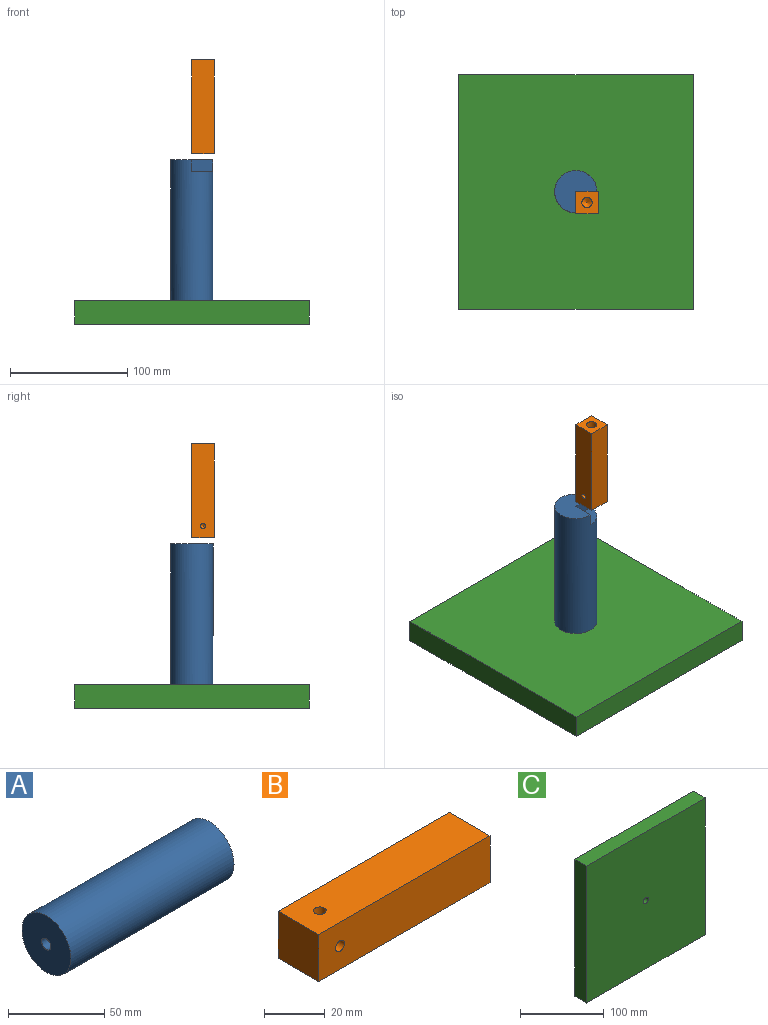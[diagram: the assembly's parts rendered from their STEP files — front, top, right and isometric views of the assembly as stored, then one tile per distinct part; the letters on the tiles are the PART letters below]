
ASSEMBLY  parts=3 mates=4
PART A: 8 faces, bbox 120x36x36 mm
  f0: cylinder r=18mm len=120mm, axis (-1,0,0), area 13288.9mm2, adj f1,f2,f5,f6,f7
  f1: plane 36x36mm, normal (-1,0,0), area 981.6mm2, adj f0,f4
  f2: plane 36x36mm, normal (1,0,0), area 763.4mm2, adj f0,f5,f6
  f3: cone r=0mm half-angle=59deg, axis (-1,0,0), area 42.4mm2, adj f4
  f4: cylinder r=3.4mm len=15.75mm, axis (-1,0,0), area 336.5mm2, adj f1,f3
  f5: plane 18x10mm, normal (0,1,0), area 180mm2, adj f0,f2,f6,f7
  f6: plane 18x10mm, normal (0,0,-1), area 180mm2, adj f0,f2,f5,f7
  f7: plane 18x18mm, normal (1,0,0), area 254.5mm2, adj f0,f5,f6
PART B: 14 faces, bbox 80x19x19 mm
  f0: plane 80x19mm, normal (0,0,1), area 1506.1mm2, adj f1,f3,f4,f5,f11
  f1: plane 19x19mm, normal (-1,0,0), area 361mm2, adj f0,f2,f4,f5
  f2: plane 80x19mm, normal (0,0,-1), area 1520mm2, adj f1,f3,f4,f5
  f3: plane 19x19mm, normal (1,0,0), area 300.2mm2, adj f0,f2,f4,f5,f7
  f4: plane 80x19mm, normal (0,-1,0), area 1506.1mm2, adj f0,f1,f2,f3,f10
  f5: plane 80x19mm, normal (0,1,0), area 1520mm2, adj f0,f1,f2,f3
  f6: cone r=0mm half-angle=59deg, axis (1,0,0), area 71mm2, adj f7
  f7: cylinder r=4.4mm len=15.75mm, axis (1,0,0), area 435.4mm2, adj f3,f6
  f8: cylinder r=2.1mm len=4.9mm, axis (0,0,1), area 47mm2, adj f9,f10,f12
  f9: cone r=0mm half-angle=59deg, axis (0,0,1), area 16.2mm2, adj f8
  f10: cylinder r=2.1mm len=9.5mm, axis (0,-1,0), area 107.7mm2, adj f4,f8,f11
  f11: cylinder r=2.1mm len=9.5mm, axis (0,0,1), area 107.7mm2, adj f0,f10,f12
  f12: cylinder r=2.1mm len=4.9mm, axis (0,-1,0), area 47mm2, adj f8,f11,f13
  f13: cone r=0mm half-angle=59deg, axis (0,-1,0), area 16.2mm2, adj f12
PART C: 9 faces, bbox 200x20x200 mm
  f0: plane 200x20mm, normal (0,0,-1), area 4000mm2, adj f1,f3,f4,f5
  f1: plane 200x20mm, normal (1,0,0), area 4000mm2, adj f0,f2,f4,f5
  f2: plane 200x20mm, normal (0,0,1), area 4000mm2, adj f1,f3,f4,f5
  f3: plane 200x20mm, normal (-1,0,0), area 4000mm2, adj f0,f2,f4,f5
  f4: plane 200x200mm, normal (0,-1,0), area 39944.6mm2, adj f0,f1,f2,f3,f6
  f5: plane 200x200mm, normal (0,1,0), area 39840.5mm2, adj f0,f1,f2,f3,f8
  f6: cylinder r=4.2mm len=12mm, axis (0,1,0), area 316.7mm2, adj f4,f7
  f7: plane 14.25x14.25mm, normal (0,1,0), area 104.1mm2, adj f6,f8
  f8: cylinder r=7.12mm len=14.25mm, axis (0,1,0), area 358.1mm2, adj f5,f7
PLACE A rot(axis=(-0.58,-0.58,-0.58),120deg) t=(-0.14,0.09,0)mm
PLACE B rot(axis=(-0.58,-0.58,-0.58),120deg) t=(9.36,-9.41,125.18)mm
PLACE C rot(axis=(-1,0,0),90deg) t=(0,0,-20)mm fixed
MATE planar B.f0 <-> A.f6  axis (0,1,0) through (9.36,0.09,165.45)mm
MATE planar A.f5 <-> B.f4  axis (1,0,0) through (-0.14,-8.91,115)mm
MATE revolute C.f6 <-> A.f3  axis (0,0,1) through (0,0,0)mm
MATE parallel A.f5 <-> C.f1  axis (1,0,0) through (-0.14,-8.91,115)mm
